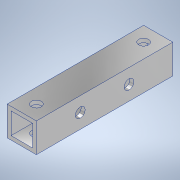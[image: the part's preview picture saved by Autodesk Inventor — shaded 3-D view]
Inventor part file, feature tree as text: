
AUTODESK INVENTOR PART (.ipt)
format: ipt  version: 2020.3 (Build 243373000, 373)  size: 131,584 bytes
history: native  units: mm
features: sketch x3, hole x2, other x1, extrude x1
ambient origin geometry x8: Origin, YZ Plane, XZ Plane, XY Plane, X Axis, Y Axis, Z Axis, Center Point
bodies: Body1 (feature_tree)
feature tree (7):
  other  "ソリッド1"
  extrude  "押し出し1"  Depth=9.0mm
  hole  "穴1"  [1 undecoded]
  hole  "穴2"  [1 undecoded]
  sketch  "スケッチ1"
  sketch  "スケッチ2"
  sketch  "スケッチ3"
note: 2 required parameter values undecoded (feature->parameter linkage not recoverable at this tier; creation-order binding heuristic only, values carry confidence <= 0.55)
